# Revit family: Haworth_BuzziCube_SoloPouf_AP_PRELIMINARY
name_source: partatom
category: Furniture
revit_build: Autodesk Revit 2018 (Build: 20170223_1515(x64)
units: mm (PartAtom-declared; Revit-internal decimal feet)

## family parameters
Always vertical = Yes
Cut with Voids When Loaded = No
OmniClass Number = 23.40.70.14.64.21
OmniClass Title = Systems Furniture
Room Calculation Point = No
Shared = No
Work Plane-Based = No

## types (2) — shared parameters
Actual Depth = 500 mm  [stored 1.64042 ft]
Actual Height = 500 mm  [stored 1.64042 ft]
Actual Width = 500 mm  [stored 1.64042 ft]
Antiskid = Yes
Assembly Code = E2020200
Base Finish = Haworth _ Polymer _ Undecided
Base Height Control = 9 mm
Description = Haworth - BuzziCube - Solo Pouf - Lounge
Manufacturer = Haworth
Model = HCBZBCX
Revision Number = 1
Size = Verify Final Dim. w/ Haworth
URL = https://www.haworth.com
URL - Product = https://www.haworth.com
Warranty = http://www.haworth.com

## per-type parameters (varying)
| type | 3D Visibility | Flat | Four Squares |
| Solo - Flat | No | Yes | No |
| Solo - Four Squares | Yes | No | Yes |

note: [stored X ft] marks values corroborated as IEEE doubles in the binary element streams (Revit-internal decimal feet)

## geometry (parser evidence)
native form markers: Sweep x12
no freeform markers — native parametric forms only
